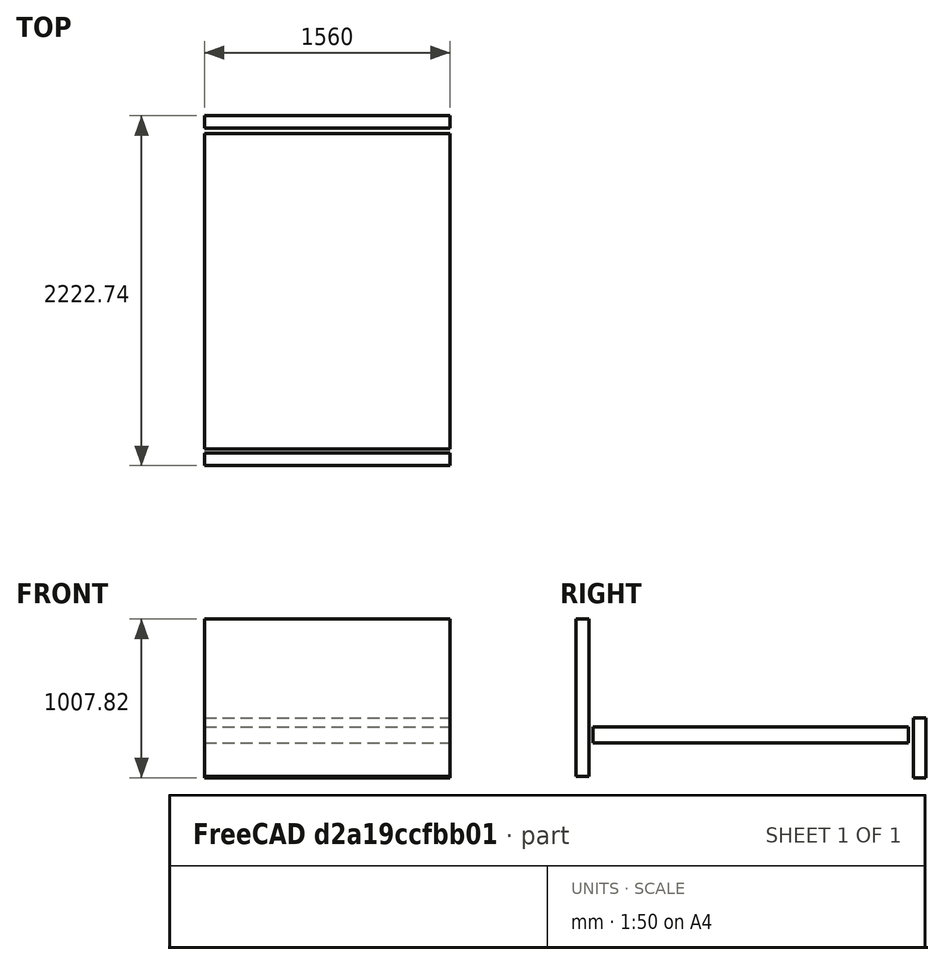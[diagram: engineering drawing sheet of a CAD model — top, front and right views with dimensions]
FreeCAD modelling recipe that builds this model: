
FCSTD DOCUMENT  (FreeCAD 1.0R38806 (Git))
Label: mueble_con_ensamblaje
License: All rights reserved
LicenseURL: https://en.wikipedia.org/wiki/All_rights_reserved
objects: Part::Box×3, App::FeaturePython×2, Assembly::JointGroup×1, Assembly::ViewGroup×1, Assembly::AssemblyObject×1
note: 3 computed .brp shape members not serialized (recipe doc carries the construction recipe); baked Part::Feature solids carry a one-line shape summary decoded from their .brp

FEATURE [Part::Box] Box  label="cabecero"
  AttacherType = Attacher::AttachEngine3D
  Height = 1000
  Length = 1560
  Placement = pos=(0,-26.3676,0) rot=(0,0,1;0rad)
  Width = 80
FEATURE [Part::Box] Box001  label="pies_de_la_cama"
  AttacherType = Attacher::AttachEngine3D
  Height = 380
  Length = 1560
  Placement = pos=(0,2116.37,-7.82195) rot=(0,0,1;0rad)
  Width = 80
FEATURE [Part::Box] Box003  label="armadura"
  AttacherType = Attacher::AttachEngine3D
  Height = 100
  Length = 1560
  Placement = pos=(0,79.9243,214.197) rot=(0,0,1;0rad)
  Width = 2004
FEATURE [Assembly::JointGroup] Joints
FEATURE [App::FeaturePython] Move  # WARN: FeaturePython — macro-defined, semantics opaque (R4)
  MoveType = 1
  MovementTransform = pos=(18,0,0) rot=(0,0,1;0rad)
  References = -> Assembly [Box.,Box001.,Box003.]
FEATURE [App::FeaturePython] Exploded_View  # WARN: FeaturePython — macro-defined, semantics opaque (R4)
  Moves = -> [Move]
FEATURE [Assembly::ViewGroup] Exploded_Views
  Group = -> [Exploded_View]
FEATURE [Assembly::AssemblyObject] Assembly
  Group = -> [Box,Joints,Box001,Box003,Exploded_Views,Exploded_View,Move]
  Origin = -> Origin
  Type = Assembly
